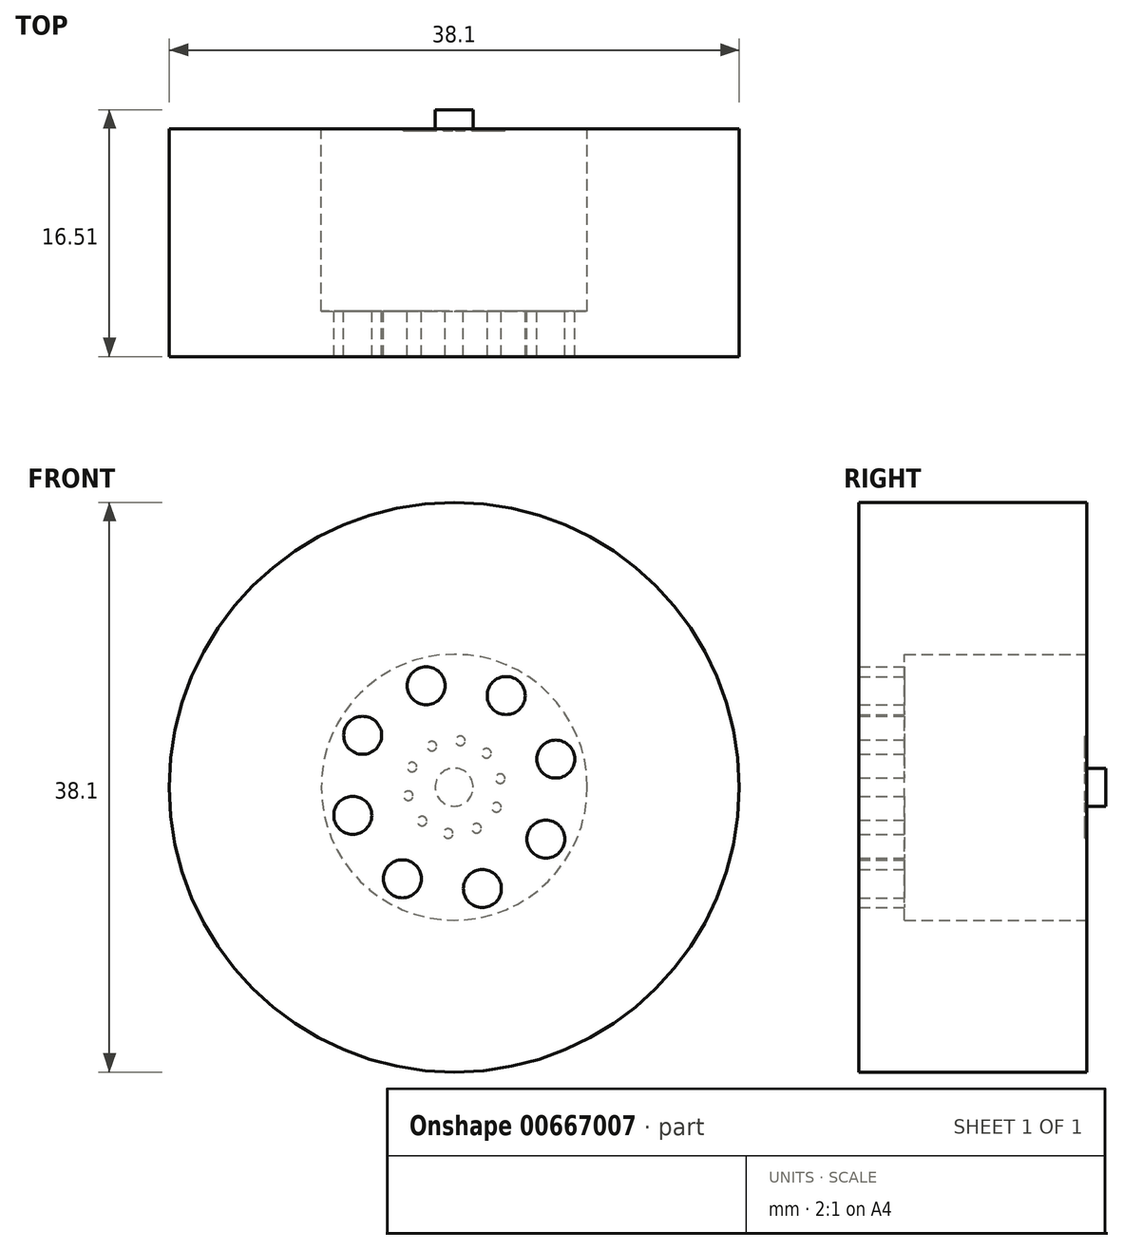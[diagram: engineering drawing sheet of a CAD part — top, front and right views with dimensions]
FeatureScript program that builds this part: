
annotation { "Feature Type Name" : "Feature", "Feature Type Description" : "" }
export const myFeature = defineFeature(function(context is Context, id is Id, definition is map)
    precondition{}
    {
        {
            var Q0;
            Q0=qCreatedBy(makeId("Front.planeOp"),FACE);
            var sketch = newSketch(context, id + "F0", { "sketchPlane" : qUnion([Q0])});
            skCircle(sketch, "E0", {"center": v(0, 0) * mm, "radius": 19.05 * mm});
            skCircle(sketch, "E1", {"center": v(0, 0) * mm, "radius": 8.9 * mm});
            skSolve(sketch);
        }
        {
            var Q0;
            Q0 = qSketchRegion(id + "F0", true);
            extrude(context, id + "F1", {"entities" : qUnion([Q0]), "depth" : 15.24 * mm, "offsetDistance" : 25.4 * mm});
        }
        {
            var Q0;
            Q0=makeQuery(id+"F0.imprint","IMPRINT",FACE,{"disambiguationData":[TD([[makeQuery(id+"F0.imprint","IMPRINT",EDGE,{"derivedFrom":sQuery(id+"F0.wireOp",EDGE,"E1")}),1.0]])]});
            extrude(context, id + "F2", {"entities" : qUnion([Q0]), "operationType" : NewBodyOperationType.ADD, "depth" : 15.24 * mm, "offsetDistance" : 25.4 * mm});
        }
        {
            var Q0;
            Q0=qCreatedBy(makeId("Front.planeOp"),FACE);
            var sketch = newSketch(context, id + "F3", { "sketchPlane" : qUnion([Q0])});
            skCircle(sketch, "E2", {"center": v(0, 0) * mm, "radius": 8.9 * mm});
            skSolve(sketch);
        }
        {
            var Q0;
            Q0 = qSketchRegion(id + "F3", true);
            extrude(context, id + "F4", {"entities" : qUnion([Q0]), "operationType" : NewBodyOperationType.REMOVE, "depth" : 12.2 * mm, "offsetDistance" : 25.4 * mm});
        }
        {
            var Q0;
            Q0=makeQuery(id+"F4.boolean.opBoolean","COPY",FACE,{"derivedFrom":makeQuery(id+"F4.opExtrude","CAP_FACE",FACE,{"disambiguationData":[OSD([sQuery(id+"F3.wireOp",EDGE,"E2")])],"isStart":false})});
            var sketch = newSketch(context, id + "F5", { "sketchPlane" : qUnion([Q0])});
            skCircle(sketch, "E3", {"center": v(-3.47, 6.13) * mm, "radius": 1.27 * mm});
            skCircle(sketch, "E4.1.0", {"center": v(-6.78, 1.88) * mm, "radius": 1.27 * mm});
            skCircle(sketch, "E4.2.0", {"center": v(-6.13, -3.47) * mm, "radius": 1.27 * mm});
            skCircle(sketch, "E4.3.0", {"center": v(-1.88, -6.78) * mm, "radius": 1.27 * mm});
            skCircle(sketch, "E4.4.0", {"center": v(3.47, -6.13) * mm, "radius": 1.27 * mm});
            skCircle(sketch, "E4.5.0", {"center": v(6.78, -1.88) * mm, "radius": 1.27 * mm});
            skCircle(sketch, "E4.6.0", {"center": v(6.13, 3.47) * mm, "radius": 1.27 * mm});
            skCircle(sketch, "E4.7.0", {"center": v(1.88, 6.78) * mm, "radius": 1.27 * mm});
            skPoint(sketch, "E4.center", {"position": v(0, 0) * mm});
            skSolve(sketch);
        }
        {
            var Q0;
            Q0=makeQuery(id+"F5.imprint","IMPRINT",FACE,{"disambiguationData":[TD([[makeQuery(id+"F5.imprint","IMPRINT",EDGE,{"derivedFrom":sQuery(id+"F5.wireOp",EDGE,"E4.1.0")}),1.0]])]});
            var Q1;
            Q1=makeQuery(id+"F5.imprint","IMPRINT",FACE,{"disambiguationData":[TD([[makeQuery(id+"F5.imprint","IMPRINT",EDGE,{"derivedFrom":sQuery(id+"F5.wireOp",EDGE,"E3")}),1.0]])]});
            var Q2;
            Q2=makeQuery(id+"F5.imprint","IMPRINT",FACE,{"disambiguationData":[TD([[makeQuery(id+"F5.imprint","IMPRINT",EDGE,{"derivedFrom":sQuery(id+"F5.wireOp",EDGE,"E4.7.0")}),1.0]])]});
            var Q3;
            Q3=makeQuery(id+"F5.imprint","IMPRINT",FACE,{"disambiguationData":[TD([[makeQuery(id+"F5.imprint","IMPRINT",EDGE,{"derivedFrom":sQuery(id+"F5.wireOp",EDGE,"E4.6.0")}),1.0]])]});
            var Q4;
            Q4=makeQuery(id+"F5.imprint","IMPRINT",FACE,{"disambiguationData":[TD([[makeQuery(id+"F5.imprint","IMPRINT",EDGE,{"derivedFrom":sQuery(id+"F5.wireOp",EDGE,"E4.4.0")}),1.0]])]});
            var Q5;
            Q5=makeQuery(id+"F5.imprint","IMPRINT",FACE,{"disambiguationData":[TD([[makeQuery(id+"F5.imprint","IMPRINT",EDGE,{"derivedFrom":sQuery(id+"F5.wireOp",EDGE,"E4.5.0")}),1.0]])]});
            var Q6;
            Q6=makeQuery(id+"F5.imprint","IMPRINT",FACE,{"disambiguationData":[TD([[makeQuery(id+"F5.imprint","IMPRINT",EDGE,{"derivedFrom":sQuery(id+"F5.wireOp",EDGE,"E4.3.0")}),1.0]])]});
            var Q7;
            Q7=makeQuery(id+"F5.imprint","IMPRINT",FACE,{"disambiguationData":[TD([[makeQuery(id+"F5.imprint","IMPRINT",EDGE,{"derivedFrom":sQuery(id+"F5.wireOp",EDGE,"E4.2.0")}),1.0]])]});
            var Q8;
            Q8=sQuery(id+"F5.wireOp",EDGE,"E4.1.0");
            extrude(context, id + "F6", {"entities" : qUnion([Q0, Q1, Q2, Q3, Q4, Q5, Q6, Q7]), "operationType" : NewBodyOperationType.REMOVE, "surfaceEntities" : qUnion([Q8]), "oppositeDirection" : true, "depth" : 3.05 * mm, "offsetDistance" : 25.4 * mm});
        }
        {
            var Q0;
            Q0=qCreatedBy(makeId("Front.planeOp"),FACE);
            var sketch = newSketch(context, id + "F7", { "sketchPlane" : qUnion([Q0])});
            skCircle(sketch, "E5", {"center": v(0, 0) * mm, "radius": 4.32 * mm});
            skCircle(sketch, "E6", {"center": v(2.15, 2.27) * mm, "radius": 0.32 * mm});
            skCircle(sketch, "E7.1.0", {"center": v(0.4, 3.1) * mm, "radius": 0.32 * mm});
            skCircle(sketch, "E7.2.0", {"center": v(-1.5, 2.75) * mm, "radius": 0.32 * mm});
            skCircle(sketch, "E7.3.0", {"center": v(-2.82, 1.34) * mm, "radius": 0.32 * mm});
            skCircle(sketch, "E7.4.0", {"center": v(-3.07, -0.57) * mm, "radius": 0.32 * mm});
            skCircle(sketch, "E7.5.0", {"center": v(-2.15, -2.27) * mm, "radius": 0.32 * mm});
            skCircle(sketch, "E7.6.0", {"center": v(-0.4, -3.1) * mm, "radius": 0.32 * mm});
            skCircle(sketch, "E7.7.0", {"center": v(1.5, -2.75) * mm, "radius": 0.32 * mm});
            skCircle(sketch, "E7.8.0", {"center": v(2.82, -1.34) * mm, "radius": 0.32 * mm});
            skCircle(sketch, "E7.9.0", {"center": v(3.07, 0.57) * mm, "radius": 0.32 * mm});
            skSolve(sketch);
        }
        {
            var Q0;
            Q0=makeQuery(id+"F7.imprint","IMPRINT",FACE,{"disambiguationData":[TD([[makeQuery(id+"F7.imprint","IMPRINT",EDGE,{"derivedFrom":sQuery(id+"F7.wireOp",EDGE,"E7.1.0")}),1.0]])]});
            var Q1;
            Q1=makeQuery(id+"F7.imprint","IMPRINT",FACE,{"disambiguationData":[TD([[makeQuery(id+"F7.imprint","IMPRINT",EDGE,{"derivedFrom":sQuery(id+"F7.wireOp",EDGE,"E6")}),1.0]])]});
            var Q2;
            Q2=makeQuery(id+"F7.imprint","IMPRINT",FACE,{"disambiguationData":[TD([[makeQuery(id+"F7.imprint","IMPRINT",EDGE,{"derivedFrom":sQuery(id+"F7.wireOp",EDGE,"E7.9.0")}),1.0]])]});
            var Q3;
            Q3=makeQuery(id+"F7.imprint","IMPRINT",FACE,{"disambiguationData":[TD([[makeQuery(id+"F7.imprint","IMPRINT",EDGE,{"derivedFrom":sQuery(id+"F7.wireOp",EDGE,"E7.8.0")}),1.0]])]});
            var Q4;
            Q4=makeQuery(id+"F7.imprint","IMPRINT",FACE,{"disambiguationData":[TD([[makeQuery(id+"F7.imprint","IMPRINT",EDGE,{"derivedFrom":sQuery(id+"F7.wireOp",EDGE,"E7.7.0")}),1.0]])]});
            var Q5;
            Q5=makeQuery(id+"F7.imprint","IMPRINT",FACE,{"disambiguationData":[TD([[makeQuery(id+"F7.imprint","IMPRINT",EDGE,{"derivedFrom":sQuery(id+"F7.wireOp",EDGE,"E7.6.0")}),1.0]])]});
            var Q6;
            Q6=makeQuery(id+"F7.imprint","IMPRINT",FACE,{"disambiguationData":[TD([[makeQuery(id+"F7.imprint","IMPRINT",EDGE,{"derivedFrom":sQuery(id+"F7.wireOp",EDGE,"E7.5.0")}),1.0]])]});
            var Q7;
            Q7=makeQuery(id+"F7.imprint","IMPRINT",FACE,{"disambiguationData":[TD([[makeQuery(id+"F7.imprint","IMPRINT",EDGE,{"derivedFrom":sQuery(id+"F7.wireOp",EDGE,"E7.4.0")}),1.0]])]});
            var Q8;
            Q8=makeQuery(id+"F7.imprint","IMPRINT",FACE,{"disambiguationData":[TD([[makeQuery(id+"F7.imprint","IMPRINT",EDGE,{"derivedFrom":sQuery(id+"F7.wireOp",EDGE,"E7.3.0")}),1.0]])]});
            var Q9;
            Q9=makeQuery(id+"F7.imprint","IMPRINT",FACE,{"disambiguationData":[TD([[makeQuery(id+"F7.imprint","IMPRINT",EDGE,{"derivedFrom":sQuery(id+"F7.wireOp",EDGE,"E7.2.0")}),1.0]])]});
            var Q10;
            Q10=makeQuery(id+"F7.imprint","IMPRINT",FACE,{"disambiguationData":[TD([[makeQuery(id+"F7.imprint","IMPRINT",EDGE,{"derivedFrom":sQuery(id+"F7.wireOp",EDGE,"E7.4.0")}),1.0]])]});
            extrude(context, id + "F8", {"entities" : qUnion([Q0, Q1, Q2, Q3, Q4, Q5, Q6, Q7, Q8, Q9, Q10]), "depth" : 0.13 * mm, "offsetDistance" : 25.4 * mm});
        }
        {
            var Q0;
            Q0=qCreatedBy(makeId("Front.planeOp"),FACE);
            var sketch = newSketch(context, id + "F9", { "sketchPlane" : qUnion([Q0])});
            skCircle(sketch, "E8", {"center": v(0, 0) * mm, "radius": 1.27 * mm});
            skSolve(sketch);
        }
        {
            var Q0;
            Q0 = qSketchRegion(id + "F9", true);
            extrude(context, id + "F10", {"entities" : qUnion([Q0]), "operationType" : NewBodyOperationType.ADD, "oppositeDirection" : true, "depth" : 1.27 * mm, "offsetDistance" : 25.4 * mm});
        }
    });
